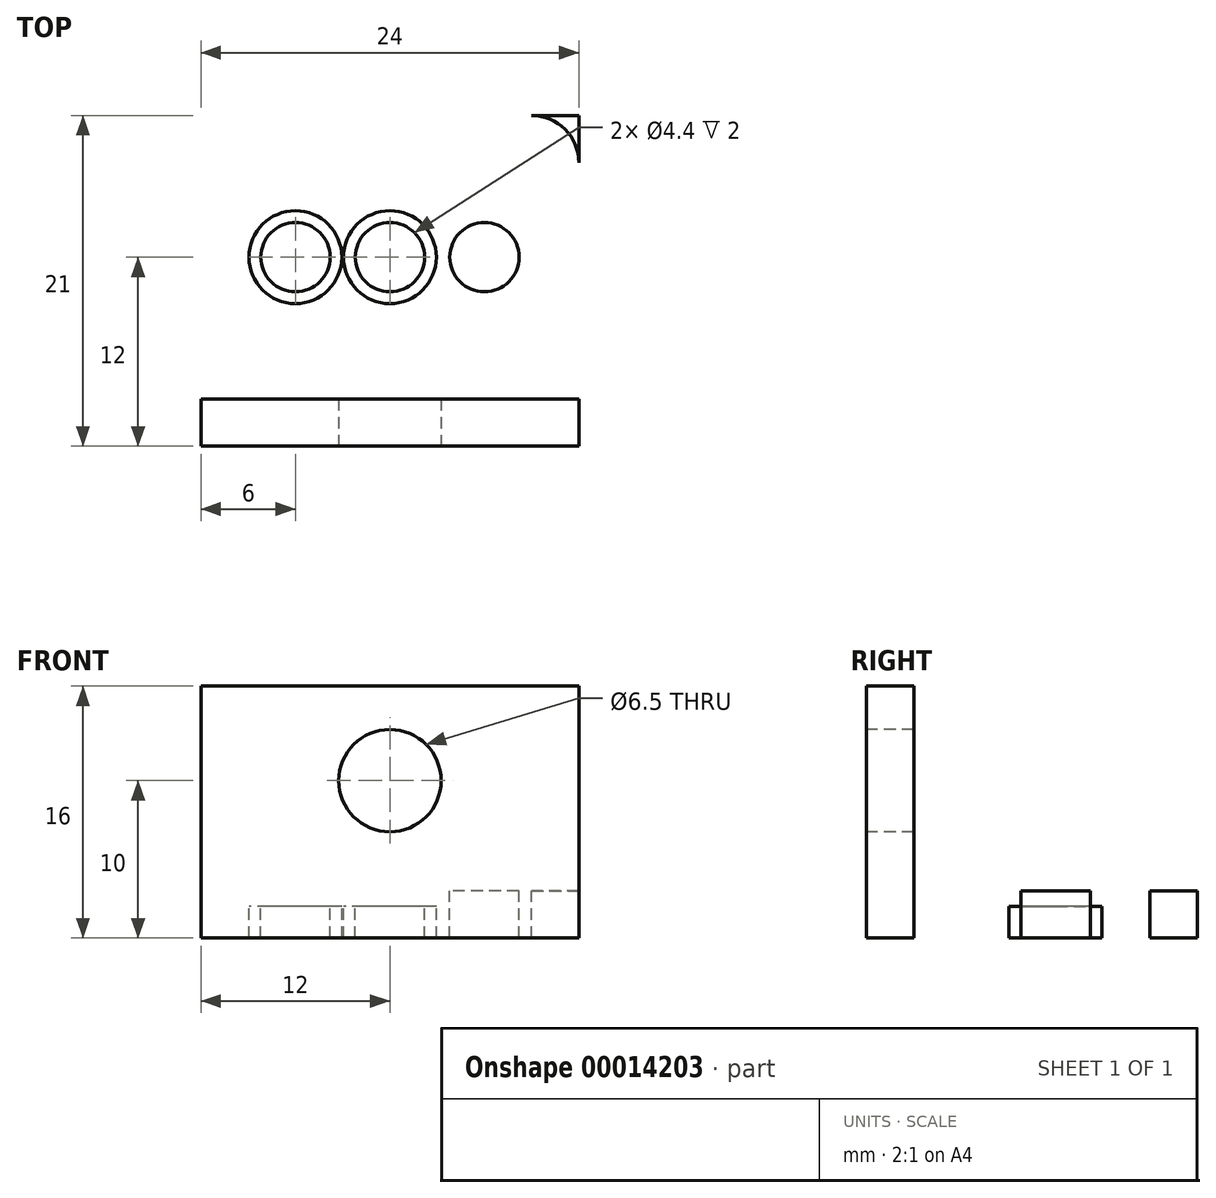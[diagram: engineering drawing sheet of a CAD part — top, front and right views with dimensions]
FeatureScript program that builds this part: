
annotation { "Feature Type Name" : "Feature", "Feature Type Description" : "" }
export const myFeature = defineFeature(function(context is Context, id is Id, definition is map)
    precondition{}
    {
        {
            var Q0;
            Q0=qCreatedBy(makeId("Front.planeOp"),FACE);
            var sketch = newSketch(context, id + "F0", { "sketchPlane" : qUnion([Q0])});
            skPoint(sketch, "E0", {"position": v(-12, 0) * mm});
            skLineSegment(sketch, "E1", {"start": v(-12, 0) * mm, "end": v(-12, -6.5) * mm});
            skLineSegment(sketch, "E2", {"start": v(-12, -6.5) * mm, "end": v(0, -6.5) * mm});
            skLineSegment(sketch, "E3.MirrorCS", {"start": v(12, 0) * mm, "end": v(12, -6.5) * mm});
            skLineSegment(sketch, "E4.MirrorCS", {"start": v(12, -6.5) * mm, "end": v(0, -6.5) * mm});
            skLineSegment(sketch, "E5.MirrorCS", {"start": v(12, 0) * mm, "end": v(12, 6.5) * mm});
            skLineSegment(sketch, "E6.MirrorCS", {"start": v(-12, 0) * mm, "end": v(-12, 6.5) * mm});
            skLineSegment(sketch, "E7.MirrorCS", {"start": v(-12, 6.5) * mm, "end": v(0, 6.5) * mm});
            skLineSegment(sketch, "E8.MirrorCS", {"start": v(12, 6.5) * mm, "end": v(0, 6.5) * mm});
            skLineSegment(sketch, "E9", {"start": v(-12, -6.5) * mm, "end": v(-12, -9.5) * mm});
            skLineSegment(sketch, "E10.MirrorCS", {"start": v(12, -6.5) * mm, "end": v(12, -9.5) * mm});
            skLineSegment(sketch, "E11", {"start": v(-12, -9.5) * mm, "end": v(12, -9.5) * mm});
            skPoint(sketch, "E12", {"position": v(0, 0.5) * mm});
            skCircle(sketch, "E13", {"center": v(0, 0.5) * mm, "radius": 3.25 * mm});
            skPoint(sketch, "E14.visualSharp", {"position": v(-12, 6.5) * mm});
            skLineSegment(sketch, "E14.filletArc", {"start": v(-12, 6.5) * mm, "end": v(-12, 6.5) * mm});
            skPoint(sketch, "E15.visualSharp", {"position": v(12, 6.5) * mm});
            skLineSegment(sketch, "E15.filletArc", {"start": v(12, 6.5) * mm, "end": v(12, 6.5) * mm});
            skSolve(sketch);
        }
        {
            var Q0;
            Q0=makeQuery(id+"F0.imprint","IMPRINT",FACE,{"disambiguationData":[TD([[makeQuery(id+"F0.imprint","IMPRINT",EDGE,{"derivedFrom":sQuery(id+"F0.wireOp",EDGE,"E1")}),1.0]])]});
            extrude(context, id + "F1", {"entities" : qUnion([Q0]), "oppositeDirection" : true, "depth" : 3 * mm});
        }
        {
            var Q0;
            Q0=makeQuery(id+"F0.imprint","IMPRINT",FACE,{"disambiguationData":[TD([[makeQuery(id+"F0.imprint","IMPRINT",EDGE,{"derivedFrom":sQuery(id+"F0.wireOp",EDGE,"E2")}),-1.0]])]});
            extrude(context, id + "F2", {"entities" : qUnion([Q0]), "operationType" : NewBodyOperationType.ADD, "oppositeDirection" : true, "depth" : 21 * mm});
        }
        {
            var Q0;
            Q0=makeQuery(id+"F2.opExtrude","SWEPT_FACE",FACE,{"disambiguationData":[OSD([sQuery(id+"F0.wireOp",EDGE,"E2"),sQuery(id+"F0.wireOp",EDGE,"E4.MirrorCS")])]});
            var sketch = newSketch(context, id + "F3", { "sketchPlane" : qUnion([Q0])});
            skLineSegment(sketch, "E16", {"start": v(-12, 12) * mm, "end": v(12, 12) * mm, "construction": true});
            skLineSegment(sketch, "E17", {"start": v(0, 3) * mm, "end": v(0, 21) * mm, "construction": true});
            skPoint(sketch, "E18", {"position": v(0, 12) * mm});
            skCircle(sketch, "E19", {"center": v(0, 12) * mm, "radius": 2.95 * mm});
            skCircle(sketch, "E20", {"center": v(0, 12) * mm, "radius": 2.2 * mm});
            skCircle(sketch, "E21", {"center": v(-6, 12) * mm, "radius": 2.95 * mm});
            skCircle(sketch, "E22", {"center": v(-6, 12) * mm, "radius": 2.2 * mm});
            skCircle(sketch, "E23.MirrorC", {"center": v(6, 12) * mm, "radius": 2.95 * mm});
            skCircle(sketch, "E24.MirrorC", {"center": v(6, 12) * mm, "radius": 2.2 * mm});
            skLineSegment(sketch, "E25", {"start": v(-12, 3) * mm, "end": v(-12, 18) * mm});
            skLineSegment(sketch, "E26", {"start": v(-9, 21) * mm, "end": v(12, 21) * mm});
            skLineSegment(sketch, "E27", {"start": v(12, 21) * mm, "end": v(12, 3) * mm});
            skLineSegment(sketch, "E28", {"start": v(12, 3) * mm, "end": v(-12, 3) * mm});
            skPoint(sketch, "E29.visualSharp", {"position": v(-12, 21) * mm});
            skArc(sketch, "E29.filletArc", {"start": v(-9, 21) * mm, "mid": v(-11.12, 20.12) * mm, "end": v(-12, 18) * mm});
            skArc(sketch, "E30.MirrorCS", {"start": v(9, 21) * mm, "mid": v(11.12, 20.12) * mm, "end": v(12, 18) * mm});
            skSolve(sketch);
        }
        {
            var Q0;
            Q0=makeQuery(id+"F3.imprint","IMPRINT",FACE,{"disambiguationData":[TD([[makeQuery(id+"F3.imprint","IMPRINT",EDGE,{"derivedFrom":sQuery(id+"F3.wireOp",EDGE,"E22")}),1.0]])]});
            var Q1;
            Q1=makeQuery(id+"F3.imprint","IMPRINT",FACE,{"disambiguationData":[TD([[makeQuery(id+"F3.imprint","IMPRINT",EDGE,{"derivedFrom":sQuery(id+"F3.wireOp",EDGE,"E20")}),1.0]])]});
            var Q2;
            Q2=makeQuery(id+"F3.imprint","IMPRINT",FACE,{"disambiguationData":[TD([[makeQuery(id+"F3.imprint","IMPRINT",EDGE,{"derivedFrom":sQuery(id+"F3.wireOp",EDGE,"E24.MirrorC")}),-1.0]])]});
            var Q3;
            {var subQ3=sQuery(id+"F3.wireOp",EDGE,"E30.MirrorCS");Q3=makeQuery(id+"F3.imprint","IMPRINT",FACE,{"disambiguationData":[TD([[makeQuery(id+"F3.imprint","IMPRINT",EDGE,{"derivedFrom":subQ3}),1.0]])]});}
            var Q4;
            {var subQ0=sQuery(id+"F3.wireOp",EDGE,"E29.filletArc");Q4=makeQuery(id+"F3.imprint","IMPRINT",FACE,{"disambiguationData":[TD([[makeQuery(id+"F3.imprint","IMPRINT",EDGE,{"derivedFrom":subQ0}),-1.0]])]});}
            extrude(context, id + "F4", {"entities" : qUnion([Q0, Q1, Q2, Q3, Q4]), "operationType" : NewBodyOperationType.REMOVE, "endBound" : BoundingType.THROUGH_ALL, "oppositeDirection" : true, "depth" : 25 * mm});
        }
        {
            var Q0;
            Q0=makeQuery(id+"F3.imprint","IMPRINT",FACE,{"disambiguationData":[TD([[makeQuery(id+"F3.imprint","IMPRINT",EDGE,{"derivedFrom":sQuery(id+"F3.wireOp",EDGE,"E21")}),1.0]])]});
            var Q1;
            Q1=makeQuery(id+"F3.imprint","IMPRINT",FACE,{"disambiguationData":[TD([[makeQuery(id+"F3.imprint","IMPRINT",EDGE,{"derivedFrom":sQuery(id+"F3.wireOp",EDGE,"E19")}),1.0]])]});
            var Q2;
            Q2=makeQuery(id+"F3.imprint","IMPRINT",FACE,{"disambiguationData":[TD([[makeQuery(id+"F3.imprint","IMPRINT",EDGE,{"derivedFrom":sQuery(id+"F3.wireOp",EDGE,"E23.MirrorC")}),-1.0]])]});
            extrude(context, id + "F5", {"entities" : qUnion([Q0, Q1, Q2]), "operationType" : NewBodyOperationType.REMOVE, "oppositeDirection" : true, "depth" : 1 * mm});
        }
    });
